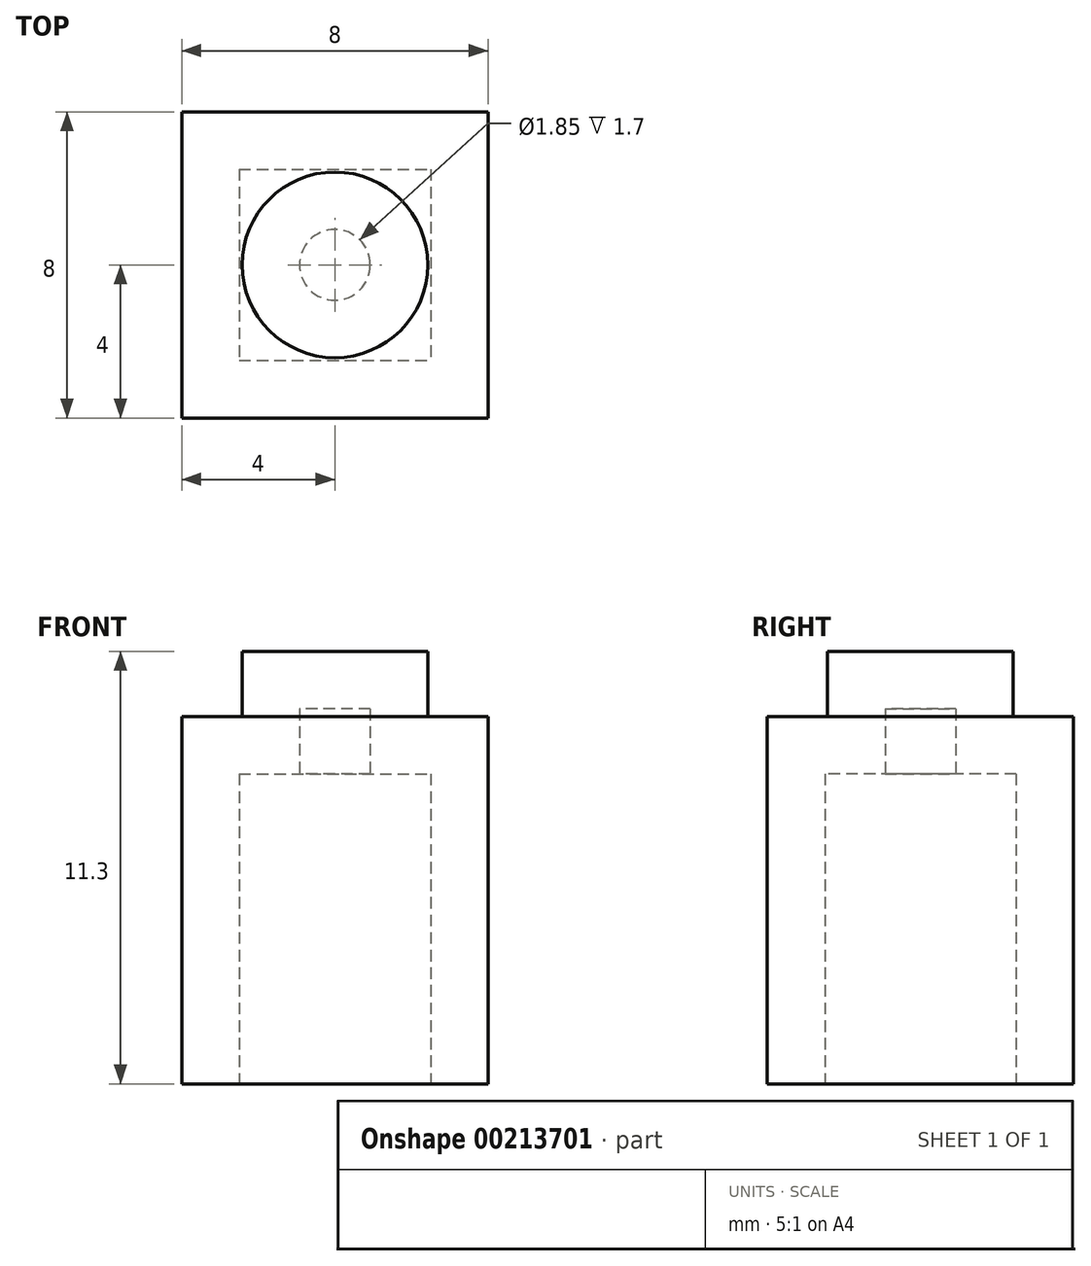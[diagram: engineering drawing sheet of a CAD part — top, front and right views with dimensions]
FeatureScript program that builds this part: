
annotation { "Feature Type Name" : "Feature", "Feature Type Description" : "" }
export const myFeature = defineFeature(function(context is Context, id is Id, definition is map)
    precondition{}
    {
        {
            var Q0;
            Q0=qCreatedBy(makeId("Top.planeOp"),FACE);
            var sketch = newSketch(context, id + "F0", { "sketchPlane" : qUnion([Q0])});
            skLineSegment(sketch, "E0.bottom", {"start": v(-4, 4) * mm, "end": v(4, 4) * mm});
            skLineSegment(sketch, "E0.top", {"start": v(-4, -4) * mm, "end": v(4, -4) * mm});
            skLineSegment(sketch, "E0.left", {"start": v(-4, 4) * mm, "end": v(-4, -4) * mm});
            skLineSegment(sketch, "E0.right", {"start": v(4, 4) * mm, "end": v(4, -4) * mm});
            skPoint(sketch, "E0.middle", {"position": v(0, 0) * mm});
            skSolve(sketch);
        }
        {
            var Q0;
            Q0=makeQuery(id+"F0.imprint","IMPRINT",FACE,{"disambiguationData":[TD([[makeQuery(id+"F0.imprint","IMPRINT",EDGE,{"derivedFrom":sQuery(id+"F0.wireOp",EDGE,"E0.bottom")}),-1.0]])]});
            extrude(context, id + "F1", {"entities" : qUnion([Q0]), "depth" : 9.6 * mm});
        }
        {
            var Q0;
            Q0=makeQuery(id+"F1.opExtrude","CAP_FACE",FACE,{"disambiguationData":[OSD([sQuery(id+"F0.wireOp",EDGE,"E0.bottom"),sQuery(id+"F0.wireOp",EDGE,"E0.top"),sQuery(id+"F0.wireOp",EDGE,"E0.left"),sQuery(id+"F0.wireOp",EDGE,"E0.right")])],"isStart":false});
            var sketch = newSketch(context, id + "F2", { "sketchPlane" : qUnion([Q0])});
            skCircle(sketch, "E1", {"center": v(0, 0) * mm, "radius": 2.42 * mm});
            skSolve(sketch);
        }
        {
            var Q0;
            {var subQ0=sQuery(id+"F2.wireOp",EDGE,"E1");var subQ1=makeQuery(id+"F2.imprint","INTERSECT",VERTEX,{"derivedFrom":[makeQuery(id+"F1.opExtrude","CAP_EDGE",EDGE,{"disambiguationData":[OSD([sQuery(id+"F0.wireOp",EDGE,"E0.bottom")])],"isStart":false}),subQ0]});Q0=makeQuery(id+"F2.imprint","IMPRINT",FACE,{"disambiguationData":[TD([[makeQuery(id+"F2.imprint","IMPRINT",EDGE,{"disambiguationData":[TD([[subQ1,1.0]])],"derivedFrom":subQ0}),1.0]])]});}
            extrude(context, id + "F3", {"entities" : qUnion([Q0]), "operationType" : NewBodyOperationType.ADD, "depth" : 1.7 * mm});
        }
        {
            var Q0;
            Q0=makeQuery(id+"F1.opExtrude","CAP_FACE",FACE,{"disambiguationData":[OSD([sQuery(id+"F0.wireOp",EDGE,"E0.bottom"),sQuery(id+"F0.wireOp",EDGE,"E0.top"),sQuery(id+"F0.wireOp",EDGE,"E0.left"),sQuery(id+"F0.wireOp",EDGE,"E0.right")])],"isStart":true});
            shell(context, id + "F4", {"entities" : qUnion([Q0]), "thickness" : 1.5 * mm});
        }
    });
